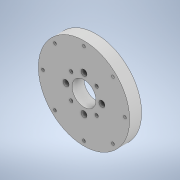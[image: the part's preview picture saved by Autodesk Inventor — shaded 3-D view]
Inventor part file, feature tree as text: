
AUTODESK INVENTOR PART (.ipt)
format: ipt  version: 2020.1 (Build 241239000, 239)  size: 160,256 bytes
history: native  units: mm
features: extrude x1, sketch x1
ambient origin geometry x8: Origin, YZ Plane, XZ Plane, XY Plane, X Axis, Y Axis, Z Axis, Center Point
bodies: Solid1 (feature_tree)
feature tree (2):
  extrude  "Extrusion1"  Depth=12.7mm
  sketch  "Sketch1"  dims[d1=97.028mm d2=25.4mm d3=38.1mm d4=6.35mm d5=6.35mm d6=6.35mm d7=6.35mm d8=3.556mm d9=3.556mm d10=3.556mm d11=3.556mm d14=45.0deg d15=45.0deg d16=45.0deg d17=87.0458mm d18=3.048mm d19=3.048mm d20=3.048mm d21=3.048mm d22=3.048mm d23=3.048mm d24=3.048mm d25=3.048mm d26=12.7mm d27=0.0mm]
